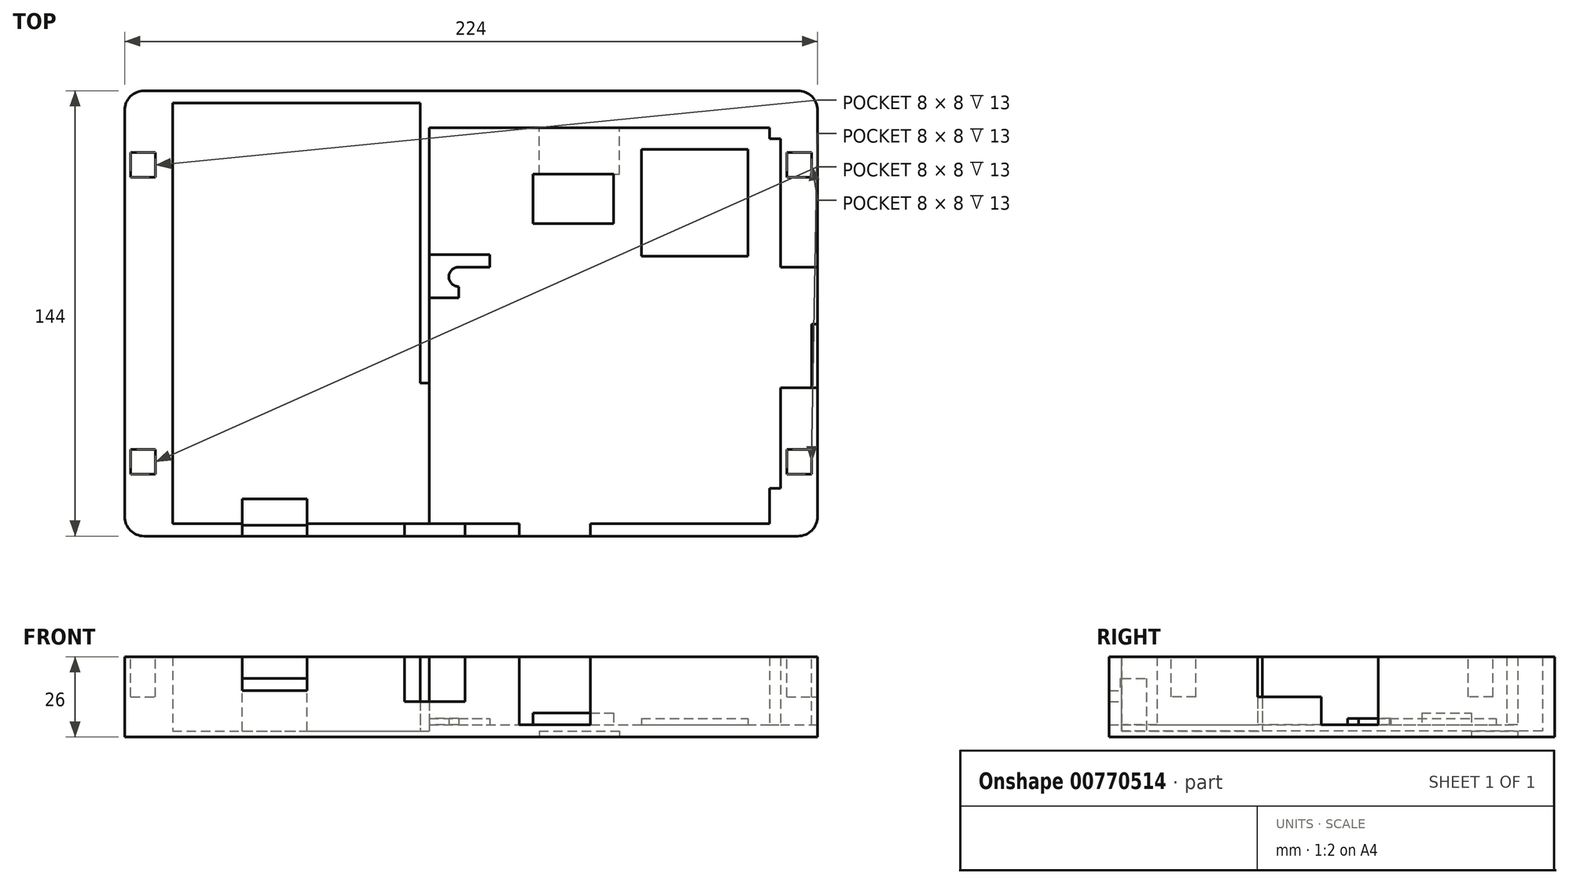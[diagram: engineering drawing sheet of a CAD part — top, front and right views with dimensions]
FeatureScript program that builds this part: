
annotation { "Feature Type Name" : "Feature", "Feature Type Description" : "" }
export const myFeature = defineFeature(function(context is Context, id is Id, definition is map)
    precondition{}
    {
        {
            var Q0;
            Q0=qCreatedBy(makeId("Top.planeOp"),FACE);
            var sketch = newSketch(context, id + "F0", { "sketchPlane" : qUnion([Q0])});
            skLineSegment(sketch, "E0.bottom", {"start": v(-224, 0) * mm, "end": v(0, 0) * mm});
            skLineSegment(sketch, "E0.top", {"start": v(-224, 144) * mm, "end": v(0, 144) * mm});
            skLineSegment(sketch, "E0.left", {"start": v(-224, 0) * mm, "end": v(-224, 144) * mm});
            skLineSegment(sketch, "E0.right", {"start": v(0, 0) * mm, "end": v(0, 144) * mm});
            skLineSegment(sketch, "E1.bottom", {"start": v(-208.5, 140) * mm, "end": v(-128.5, 140) * mm});
            skLineSegment(sketch, "E1.top", {"start": v(-208.5, 4) * mm, "end": v(-186, 4) * mm});
            skLineSegment(sketch, "E1.left", {"start": v(-208.5, 140) * mm, "end": v(-208.5, 4) * mm});
            skLineSegment(sketch, "E1.right", {"start": v(-12, 128.5) * mm, "end": v(-12, 15.5) * mm});
            skLineSegment(sketch, "E2", {"start": v(-128.5, 140) * mm, "end": v(-128.5, 49.5) * mm});
            skLineSegment(sketch, "E3", {"start": v(-128.5, 49.5) * mm, "end": v(-125.5, 49.5) * mm});
            skLineSegment(sketch, "E4", {"start": v(-125.5, 49.5) * mm, "end": v(-125.5, 132) * mm});
            skLineSegment(sketch, "E5.bottom", {"start": v(-222, 124) * mm, "end": v(-214, 124) * mm});
            skLineSegment(sketch, "E5.top", {"start": v(-222, 116) * mm, "end": v(-214, 116) * mm});
            skLineSegment(sketch, "E5.left", {"start": v(-222, 124) * mm, "end": v(-222, 116) * mm});
            skLineSegment(sketch, "E5.right", {"start": v(-214, 124) * mm, "end": v(-214, 116) * mm});
            skLineSegment(sketch, "E6.bottom", {"start": v(-222, 28) * mm, "end": v(-214, 28) * mm});
            skLineSegment(sketch, "E6.top", {"start": v(-222, 20) * mm, "end": v(-214, 20) * mm});
            skLineSegment(sketch, "E6.left", {"start": v(-222, 28) * mm, "end": v(-222, 20) * mm});
            skLineSegment(sketch, "E6.right", {"start": v(-214, 28) * mm, "end": v(-214, 20) * mm});
            skLineSegment(sketch, "E7", {"start": v(-165, 0) * mm, "end": v(-165, 12) * mm});
            skLineSegment(sketch, "E8.trimOffspring", {"start": v(-165, 4) * mm, "end": v(-15.5, 4) * mm});
            skLineSegment(sketch, "E9", {"start": v(-186, 0) * mm, "end": v(-186, 12) * mm});
            skLineSegment(sketch, "E10", {"start": v(-175.5, 30.08) * mm, "end": v(-175.5, -46.23) * mm, "construction": true});
            skLineSegment(sketch, "E11", {"start": v(-186, 12) * mm, "end": v(-165, 12) * mm});
            skLineSegment(sketch, "E12", {"start": v(-133.5, 4) * mm, "end": v(-133.5, 0) * mm});
            skLineSegment(sketch, "E13", {"start": v(-114, 4) * mm, "end": v(-114, 0) * mm});
            skLineSegment(sketch, "E14", {"start": v(-73.4, 4) * mm, "end": v(-73.4, 0) * mm});
            skLineSegment(sketch, "E15", {"start": v(-96.4, 4) * mm, "end": v(-96.4, 0) * mm});
            skLineSegment(sketch, "E16.bottom", {"start": v(-10, 28) * mm, "end": v(-2, 28) * mm});
            skLineSegment(sketch, "E16.top", {"start": v(-10, 20) * mm, "end": v(-2, 20) * mm});
            skLineSegment(sketch, "E16.left", {"start": v(-10, 28) * mm, "end": v(-10, 20) * mm});
            skLineSegment(sketch, "E16.right", {"start": v(-2, 28) * mm, "end": v(-2, 20) * mm});
            skLineSegment(sketch, "E17.bottom", {"start": v(-10, 124) * mm, "end": v(-2, 124) * mm});
            skLineSegment(sketch, "E17.top", {"start": v(-10, 116) * mm, "end": v(-2, 116) * mm});
            skLineSegment(sketch, "E17.left", {"start": v(-10, 124) * mm, "end": v(-10, 116) * mm});
            skLineSegment(sketch, "E17.right", {"start": v(-2, 124) * mm, "end": v(-2, 116) * mm});
            skLineSegment(sketch, "E18", {"start": v(-15.5, 132) * mm, "end": v(-15.5, 128.5) * mm});
            skLineSegment(sketch, "E19", {"start": v(-15.5, 128.5) * mm, "end": v(-12, 128.5) * mm});
            skLineSegment(sketch, "E20", {"start": v(-12, 15.5) * mm, "end": v(-15.5, 15.5) * mm});
            skLineSegment(sketch, "E21", {"start": v(-15.5, 15.5) * mm, "end": v(-15.5, 4) * mm});
            skLineSegment(sketch, "E22", {"start": v(-15.5, 132) * mm, "end": v(-125.5, 132) * mm});
            skLineSegment(sketch, "E23.bottom", {"start": v(-57, 125) * mm, "end": v(-22, 125) * mm});
            skLineSegment(sketch, "E23.top", {"start": v(-57, 90.5) * mm, "end": v(-22, 90.5) * mm});
            skLineSegment(sketch, "E23.left", {"start": v(-57, 125) * mm, "end": v(-57, 90.5) * mm});
            skLineSegment(sketch, "E24.bottom", {"start": v(-60, 89) * mm, "end": v(-17.5, 89) * mm, "construction": true});
            skLineSegment(sketch, "E24.top", {"start": v(-60, 132) * mm, "end": v(-17.5, 132) * mm, "construction": true});
            skLineSegment(sketch, "E24.left", {"start": v(-60, 89) * mm, "end": v(-60, 132) * mm, "construction": true});
            skLineSegment(sketch, "E24.right", {"start": v(-17.5, 89) * mm, "end": v(-17.5, 132) * mm, "construction": true});
            skLineSegment(sketch, "E25.bottom", {"start": v(-90, 96) * mm, "end": v(-64, 96) * mm});
            skLineSegment(sketch, "E25.top", {"start": v(-90, 132) * mm, "end": v(-64, 132) * mm});
            skLineSegment(sketch, "E25.left", {"start": v(-90, 96) * mm, "end": v(-90, 132) * mm});
            skLineSegment(sketch, "E25.right", {"start": v(-64, 96) * mm, "end": v(-64, 132) * mm});
            skLineSegment(sketch, "E26", {"start": v(-125.5, 49.5) * mm, "end": v(-116, 49.5) * mm});
            skLineSegment(sketch, "E27", {"start": v(-116, 87) * mm, "end": v(-116, 49.5) * mm});
            skLineSegment(sketch, "E28", {"start": v(-116, 87) * mm, "end": v(-125.5, 87) * mm});
            skLineSegment(sketch, "E29", {"start": v(-116, 87) * mm, "end": v(0, 87) * mm});
            skLineSegment(sketch, "E30", {"start": v(-12, 50) * mm, "end": v(0, 50) * mm});
            skLineSegment(sketch, "E31", {"start": v(-128.5, 49.5) * mm, "end": v(-128.5, 4) * mm});
            skPoint(sketch, "E32.startSnap0", {"position": v(-112, 144) * mm});
            skLineSegment(sketch, "E33.bottom", {"start": v(-90, 101) * mm, "end": v(-64, 101) * mm});
            skLineSegment(sketch, "E33.top", {"start": v(-90, 117) * mm, "end": v(-64, 117) * mm});
            skLineSegment(sketch, "E33.left", {"start": v(-90, 101) * mm, "end": v(-90, 117) * mm});
            skLineSegment(sketch, "E33.right", {"start": v(-64, 101) * mm, "end": v(-64, 117) * mm});
            skLineSegment(sketch, "E34", {"start": v(-22, 125) * mm, "end": v(-22, 90.5) * mm});
            skLineSegment(sketch, "E35", {"start": v(-196, 0) * mm, "end": v(-196, 4) * mm, "construction": true});
            skSolve(sketch);
        }
        {
            var Q0;
            {var subQ14=sQuery(id+"F0.wireOp",EDGE,"E0.top");Q0=makeQuery(id+"F0.imprint","IMPRINT",FACE,{"disambiguationData":[TD([[makeQuery(id+"F0.imprint","IMPRINT",EDGE,{"derivedFrom":subQ14}),-1.0]])]});}
            var Q1;
            Q1=makeQuery(id+"F0.imprint","IMPRINT",FACE,{"disambiguationData":[TD([[makeQuery(id+"F0.imprint","IMPRINT",EDGE,{"derivedFrom":sQuery(id+"F0.wireOp",EDGE,"E1.bottom")}),-1.0]])]});
            var Q2;
            {var subQ5=sQuery(id+"F0.wireOp",EDGE,"E1.top");Q2=makeQuery(id+"F0.imprint","IMPRINT",FACE,{"disambiguationData":[TD([[makeQuery(id+"F0.imprint","IMPRINT",EDGE,{"derivedFrom":subQ5}),-1.0]])]});}
            var Q3;
            {var subQ0=sQuery(id+"F0.wireOp",EDGE,"E12");Q3=makeQuery(id+"F0.imprint","IMPRINT",FACE,{"disambiguationData":[TD([[makeQuery(id+"F0.imprint","IMPRINT",EDGE,{"derivedFrom":subQ0}),1.0]])]});}
            var Q4;
            {var subQ0=sQuery(id+"F0.wireOp",EDGE,"E15");Q4=makeQuery(id+"F0.imprint","IMPRINT",FACE,{"disambiguationData":[TD([[makeQuery(id+"F0.imprint","IMPRINT",EDGE,{"derivedFrom":subQ0}),-1.0]])]});}
            var Q5;
            {var subQ3=sQuery(id+"F0.wireOp",EDGE,"E12");Q5=makeQuery(id+"F0.imprint","IMPRINT",FACE,{"disambiguationData":[TD([[makeQuery(id+"F0.imprint","IMPRINT",EDGE,{"derivedFrom":subQ3}),-1.0]])]});}
            var Q6;
            {var subQ7=sQuery(id+"F0.wireOp",EDGE,"E11");Q6=makeQuery(id+"F0.imprint","IMPRINT",FACE,{"disambiguationData":[TD([[makeQuery(id+"F0.imprint","IMPRINT",EDGE,{"derivedFrom":subQ7}),-1.0]])]});}
            var Q7;
            {var subQ0=sQuery(id+"F0.wireOp",EDGE,"E26");Q7=makeQuery(id+"F0.imprint","IMPRINT",FACE,{"disambiguationData":[TD([[makeQuery(id+"F0.imprint","IMPRINT",EDGE,{"derivedFrom":subQ0}),1.0]])]});}
            var Q8;
            {var subQ11=sQuery(id+"F0.wireOp",EDGE,"E18");Q8=makeQuery(id+"F0.imprint","IMPRINT",FACE,{"disambiguationData":[TD([[makeQuery(id+"F0.imprint","IMPRINT",EDGE,{"derivedFrom":subQ11}),-1.0]])]});}
            var Q9;
            {var subQ0=sQuery(id+"F0.wireOp",EDGE,"E25.top");Q9=makeQuery(id+"F0.imprint","IMPRINT",FACE,{"disambiguationData":[TD([[makeQuery(id+"F0.imprint","IMPRINT",EDGE,{"derivedFrom":subQ0}),-1.0]])]});}
            var Q10;
            Q10=makeQuery(id+"F0.imprint","IMPRINT",FACE,{"disambiguationData":[TD([[makeQuery(id+"F0.imprint","IMPRINT",EDGE,{"derivedFrom":sQuery(id+"F0.wireOp",EDGE,"E33.bottom")}),1.0]])]});
            var Q11;
            {var subQ0=sQuery(id+"F0.wireOp",EDGE,"E25.bottom");Q11=makeQuery(id+"F0.imprint","IMPRINT",FACE,{"disambiguationData":[TD([[makeQuery(id+"F0.imprint","IMPRINT",EDGE,{"derivedFrom":subQ0}),1.0]])]});}
            var Q12;
            Q12=makeQuery(id+"F0.imprint","IMPRINT",FACE,{"disambiguationData":[TD([[makeQuery(id+"F0.imprint","IMPRINT",EDGE,{"derivedFrom":sQuery(id+"F0.wireOp",EDGE,"E23.bottom")}),-1.0]])]});
            var Q13;
            Q13=makeQuery(id+"F0.imprint","IMPRINT",FACE,{"disambiguationData":[TD([[makeQuery(id+"F0.imprint","IMPRINT",EDGE,{"derivedFrom":sQuery(id+"F0.wireOp",EDGE,"E17.bottom")}),-1.0]])]});
            var Q14;
            Q14=makeQuery(id+"F0.imprint","IMPRINT",FACE,{"disambiguationData":[TD([[makeQuery(id+"F0.imprint","IMPRINT",EDGE,{"derivedFrom":sQuery(id+"F0.wireOp",EDGE,"E5.bottom")}),-1.0]])]});
            var Q15;
            Q15=makeQuery(id+"F0.imprint","IMPRINT",FACE,{"disambiguationData":[TD([[makeQuery(id+"F0.imprint","IMPRINT",EDGE,{"derivedFrom":sQuery(id+"F0.wireOp",EDGE,"E6.bottom")}),-1.0]])]});
            var Q16;
            {var subQ0=sQuery(id+"F0.wireOp",EDGE,"E30");var subQ1=sQuery(id+"F0.wireOp",EDGE,"E0.right");var subQ2=makeQuery(id+"F0.imprint","INTERSECT",VERTEX,{"derivedFrom":[subQ1,subQ0]});Q16=makeQuery(id+"F0.imprint","IMPRINT",FACE,{"disambiguationData":[TD([[makeQuery(id+"F0.imprint","IMPRINT",EDGE,{"disambiguationData":[TD([[subQ2,-1.0]])],"derivedFrom":subQ1}),1.0]])]});}
            var Q17;
            Q17=makeQuery(id+"F0.imprint","IMPRINT",FACE,{"disambiguationData":[TD([[makeQuery(id+"F0.imprint","IMPRINT",EDGE,{"derivedFrom":sQuery(id+"F0.wireOp",EDGE,"E3")}),-1.0]])]});
            var Q18;
            {var subQ6=sQuery(id+"F0.wireOp",EDGE,"E14");Q18=makeQuery(id+"F0.imprint","IMPRINT",FACE,{"disambiguationData":[TD([[makeQuery(id+"F0.imprint","IMPRINT",EDGE,{"derivedFrom":subQ6}),1.0]])]});}
            var Q19;
            Q19=makeQuery(id+"F0.imprint","IMPRINT",FACE,{"disambiguationData":[TD([[makeQuery(id+"F0.imprint","IMPRINT",EDGE,{"derivedFrom":sQuery(id+"F0.wireOp",EDGE,"E16.bottom")}),-1.0]])]});
            var Q20;
            {var subQ0=sQuery(id+"F0.wireOp",EDGE,"E14");Q20=makeQuery(id+"F0.imprint","IMPRINT",FACE,{"disambiguationData":[TD([[makeQuery(id+"F0.imprint","IMPRINT",EDGE,{"derivedFrom":subQ0}),-1.0]])]});}
            extrude(context, id + "F1", {"entities" : qUnion([Q0, Q1, Q2, Q3, Q4, Q5, Q6, Q7, Q8, Q9, Q10, Q11, Q12, Q13, Q14, Q15, Q16, Q17, Q18, Q19, Q20]), "depth" : 2 * mm, "offsetDistance" : 25 * mm});
        }
        {
            var Q0;
            Q0=makeQuery(id+"F1.opExtrude","CAP_FACE",FACE,{"disambiguationData":[OSD([sQuery(id+"F0.wireOp",EDGE,"E0.bottom"),sQuery(id+"F0.wireOp",EDGE,"E0.top"),sQuery(id+"F0.wireOp",EDGE,"E0.left"),sQuery(id+"F0.wireOp",EDGE,"E0.right")])],"isStart":false});
            var sketch = newSketch(context, id + "F2", { "sketchPlane" : qUnion([Q0])});
            skLineSegment(sketch, "E36.bottom", {"start": v(-224, 0) * mm, "end": v(0, 0) * mm});
            skLineSegment(sketch, "E36.top", {"start": v(-224, 144) * mm, "end": v(0, 144) * mm});
            skLineSegment(sketch, "E36.left", {"start": v(-224, 0) * mm, "end": v(-224, 144) * mm});
            skLineSegment(sketch, "E36.right", {"start": v(0, 0) * mm, "end": v(0, 144) * mm});
            skLineSegment(sketch, "E37", {"start": v(-208.5, 140) * mm, "end": v(-208.5, 4) * mm});
            skLineSegment(sketch, "E38", {"start": v(-208.5, 4) * mm, "end": v(-15.5, 4) * mm});
            skLineSegment(sketch, "E39", {"start": v(-208.5, 140) * mm, "end": v(-128.5, 140) * mm});
            skLineSegment(sketch, "E40", {"start": v(-128.5, 140) * mm, "end": v(-128.5, 49.5) * mm});
            skLineSegment(sketch, "E41", {"start": v(-128.5, 49.5) * mm, "end": v(-125.5, 49.5) * mm});
            skLineSegment(sketch, "E42", {"start": v(-125.5, 49.5) * mm, "end": v(-125.5, 132) * mm});
            skLineSegment(sketch, "E43", {"start": v(-125.5, 132) * mm, "end": v(-15.5, 132) * mm});
            skLineSegment(sketch, "E44", {"start": v(-15.5, 132) * mm, "end": v(-15.5, 128.5) * mm});
            skLineSegment(sketch, "E45", {"start": v(-15.5, 128.5) * mm, "end": v(-12, 128.5) * mm});
            skLineSegment(sketch, "E46", {"start": v(-12, 128.5) * mm, "end": v(-12, 87) * mm});
            skLineSegment(sketch, "E47", {"start": v(-12, 87) * mm, "end": v(-2, 87) * mm});
            skLineSegment(sketch, "E48", {"start": v(-2, 87) * mm, "end": v(-2, 50) * mm});
            skLineSegment(sketch, "E49", {"start": v(-2, 50) * mm, "end": v(-12, 50) * mm, "construction": true});
            skLineSegment(sketch, "E50", {"start": v(-12, 48) * mm, "end": v(-12, 15.5) * mm});
            skLineSegment(sketch, "E51", {"start": v(-12, 15.5) * mm, "end": v(-15.5, 15.5) * mm});
            skLineSegment(sketch, "E52", {"start": v(-15.5, 15.5) * mm, "end": v(-15.5, 4) * mm});
            skLineSegment(sketch, "E53", {"start": v(-12, 48) * mm, "end": v(-2, 48) * mm});
            skLineSegment(sketch, "E54", {"start": v(-2, 48) * mm, "end": v(-2, 50) * mm});
            skSolve(sketch);
        }
        {
            var Q0;
            Q0=qSketchRegion(id+"F2",true);
            extrude(context, id + "F3", {"entities" : qUnion([Q0]), "operationType" : NewBodyOperationType.ADD, "depth" : 24 * mm, "offsetDistance" : 25 * mm});
        }
        {
            var Q0;
            Q0=makeQuery(id+"F3.opExtrude","CAP_FACE",FACE,{"disambiguationData":[OSD([sQuery(id+"F2.wireOp",EDGE,"E36.bottom"),sQuery(id+"F2.wireOp",EDGE,"E36.top"),sQuery(id+"F2.wireOp",EDGE,"E36.left"),sQuery(id+"F2.wireOp",EDGE,"E36.right"),sQuery(id+"F2.wireOp",EDGE,"E37"),sQuery(id+"F2.wireOp",EDGE,"E38"),sQuery(id+"F2.wireOp",EDGE,"E39"),sQuery(id+"F2.wireOp",EDGE,"E40"),sQuery(id+"F2.wireOp",EDGE,"E41"),sQuery(id+"F2.wireOp",EDGE,"E42"),sQuery(id+"F2.wireOp",EDGE,"E43"),sQuery(id+"F2.wireOp",EDGE,"E44"),sQuery(id+"F2.wireOp",EDGE,"E45"),sQuery(id+"F2.wireOp",EDGE,"E46"),sQuery(id+"F2.wireOp",EDGE,"E47"),sQuery(id+"F2.wireOp",EDGE,"E48"),sQuery(id+"F2.wireOp",EDGE,"E49"),sQuery(id+"F2.wireOp",EDGE,"E50"),sQuery(id+"F2.wireOp",EDGE,"E51"),sQuery(id+"F2.wireOp",EDGE,"E52")])],"isStart":false});
            var sketch = newSketch(context, id + "F4", { "sketchPlane" : qUnion([Q0])});
            skLineSegment(sketch, "E55.bottom", {"start": v(-186, 0) * mm, "end": v(-165, 0) * mm});
            skLineSegment(sketch, "E55.top", {"start": v(-186, 4) * mm, "end": v(-165, 4) * mm});
            skLineSegment(sketch, "E55.left", {"start": v(-186, 0) * mm, "end": v(-186, 4) * mm});
            skLineSegment(sketch, "E55.right", {"start": v(-165, 0) * mm, "end": v(-165, 4) * mm});
            skSolve(sketch);
        }
        {
            var Q0;
            Q0=qSketchRegion(id+"F4",true);
            extrude(context, id + "F5", {"entities" : qUnion([Q0]), "operationType" : NewBodyOperationType.REMOVE, "oppositeDirection" : true, "depth" : 11 * mm, "offsetDistance" : 25 * mm});
        }
        {
            var Q0;
            Q0=makeQuery(id+"F1.opExtrude","CAP_FACE",FACE,{"disambiguationData":[OSD([sQuery(id+"F0.wireOp",EDGE,"E0.bottom"),sQuery(id+"F0.wireOp",EDGE,"E0.top"),sQuery(id+"F0.wireOp",EDGE,"E0.left"),sQuery(id+"F0.wireOp",EDGE,"E0.right")])],"isStart":false});
            var sketch = newSketch(context, id + "F6", { "sketchPlane" : qUnion([Q0])});
            skLineSegment(sketch, "E56.bottom", {"start": v(-186, 3.5) * mm, "end": v(-165, 3.5) * mm});
            skLineSegment(sketch, "E56.top", {"start": v(-186, 12) * mm, "end": v(-165, 12) * mm});
            skLineSegment(sketch, "E56.left", {"start": v(-186, 3.5) * mm, "end": v(-186, 12) * mm});
            skLineSegment(sketch, "E56.right", {"start": v(-165, 3.5) * mm, "end": v(-165, 12) * mm});
            skSolve(sketch);
        }
        {
            var Q0;
            Q0=qSketchRegion(id+"F6",true);
            extrude(context, id + "F7", {"entities" : qUnion([Q0]), "operationType" : NewBodyOperationType.ADD, "depth" : 17 * mm, "offsetDistance" : 25 * mm});
        }
        {
            var Q0;
            Q0=makeQuery(id+"F3.boolean.opBoolean","MERGE",EDGE,{"derivedFrom":[makeQuery(id+"F1.opExtrude","SWEPT_EDGE",EDGE,{"disambiguationData":[OSD([sQuery(id+"F0.wireOp",EDGE,"E0.bottom"),sQuery(id+"F0.wireOp",EDGE,"E0.left")])]}),makeQuery(id+"F3.opExtrude","SWEPT_EDGE",EDGE,{"disambiguationData":[OSD([sQuery(id+"F2.wireOp",EDGE,"E36.bottom"),sQuery(id+"F2.wireOp",EDGE,"E36.left")])]})]});
            var Q1;
            Q1=makeQuery(id+"F3.boolean.opBoolean","MERGE",EDGE,{"derivedFrom":[makeQuery(id+"F1.opExtrude","SWEPT_EDGE",EDGE,{"disambiguationData":[OSD([sQuery(id+"F0.wireOp",EDGE,"E0.bottom"),sQuery(id+"F0.wireOp",EDGE,"E0.right")])]}),makeQuery(id+"F3.opExtrude","SWEPT_EDGE",EDGE,{"disambiguationData":[OSD([sQuery(id+"F2.wireOp",EDGE,"E36.bottom"),sQuery(id+"F2.wireOp",EDGE,"E36.right")])]})]});
            var Q2;
            Q2=makeQuery(id+"F3.boolean.opBoolean","MERGE",EDGE,{"derivedFrom":[makeQuery(id+"F1.opExtrude","SWEPT_EDGE",EDGE,{"disambiguationData":[OSD([sQuery(id+"F0.wireOp",EDGE,"E0.top"),sQuery(id+"F0.wireOp",EDGE,"E0.right")])]}),makeQuery(id+"F3.opExtrude","SWEPT_EDGE",EDGE,{"disambiguationData":[OSD([sQuery(id+"F2.wireOp",EDGE,"E36.top"),sQuery(id+"F2.wireOp",EDGE,"E36.right")])]})]});
            var Q3;
            Q3=makeQuery(id+"F3.boolean.opBoolean","MERGE",EDGE,{"derivedFrom":[makeQuery(id+"F1.opExtrude","SWEPT_EDGE",EDGE,{"disambiguationData":[OSD([sQuery(id+"F0.wireOp",EDGE,"E0.top"),sQuery(id+"F0.wireOp",EDGE,"E0.left")])]}),makeQuery(id+"F3.opExtrude","SWEPT_EDGE",EDGE,{"disambiguationData":[OSD([sQuery(id+"F2.wireOp",EDGE,"E36.top"),sQuery(id+"F2.wireOp",EDGE,"E36.left")])]})]});
            fillet(context, id + "F8", {"entities" : qUnion([Q0, Q1, Q2, Q3]), "radius" : 6.35 * mm, "tangentPropagation" : true, "allowEdgeOverflow" : false});
        }
        {
            var Q0;
            Q0=makeQuery(id+"F1.opExtrude","CAP_FACE",FACE,{"disambiguationData":[OSD([sQuery(id+"F0.wireOp",EDGE,"E0.bottom"),sQuery(id+"F0.wireOp",EDGE,"E0.top"),sQuery(id+"F0.wireOp",EDGE,"E0.left"),sQuery(id+"F0.wireOp",EDGE,"E0.right")])],"isStart":false});
            var sketch = newSketch(context, id + "F9", { "sketchPlane" : qUnion([Q0])});
            skLineSegment(sketch, "E57.bottom", {"start": v(-57, 90.5) * mm, "end": v(-22.5, 90.5) * mm});
            skLineSegment(sketch, "E57.top", {"start": v(-57, 125) * mm, "end": v(-22.5, 125) * mm});
            skLineSegment(sketch, "E57.left", {"start": v(-57, 90.5) * mm, "end": v(-57, 125) * mm});
            skLineSegment(sketch, "E57.right", {"start": v(-22.5, 90.5) * mm, "end": v(-22.5, 125) * mm});
            skLineSegment(sketch, "E58.bottom", {"start": v(-60, 87) * mm, "end": v(-15, 87) * mm, "construction": true});
            skLineSegment(sketch, "E58.top", {"start": v(-60, 132) * mm, "end": v(-15, 132) * mm, "construction": true});
            skLineSegment(sketch, "E58.left", {"start": v(-60, 87) * mm, "end": v(-60, 132) * mm, "construction": true});
            skLineSegment(sketch, "E58.right", {"start": v(-15, 87) * mm, "end": v(-15, 132) * mm, "construction": true});
            skSolve(sketch);
        }
        {
            var Q0;
            Q0=qSketchRegion(id+"F9",true);
            extrude(context, id + "F10", {"entities" : qUnion([Q0]), "operationType" : NewBodyOperationType.ADD, "depth" : 4 * mm, "offsetDistance" : 25 * mm});
        }
        {
            var Q0;
            Q0=makeQuery(id+"F1.opExtrude","CAP_FACE",FACE,{"disambiguationData":[OSD([sQuery(id+"F0.wireOp",EDGE,"E0.bottom"),sQuery(id+"F0.wireOp",EDGE,"E0.top"),sQuery(id+"F0.wireOp",EDGE,"E0.left"),sQuery(id+"F0.wireOp",EDGE,"E0.right")])],"isStart":false});
            var sketch = newSketch(context, id + "F11", { "sketchPlane" : qUnion([Q0])});
            skLineSegment(sketch, "E59.bottom", {"start": v(-92, 101) * mm, "end": v(-66, 101) * mm});
            skLineSegment(sketch, "E59.top", {"start": v(-92, 117) * mm, "end": v(-66, 117) * mm});
            skLineSegment(sketch, "E59.left", {"start": v(-92, 101) * mm, "end": v(-92, 117) * mm});
            skLineSegment(sketch, "E59.right", {"start": v(-66, 101) * mm, "end": v(-66, 117) * mm});
            skSolve(sketch);
        }
        {
            var Q0;
            Q0=qSketchRegion(id+"F11",true);
            extrude(context, id + "F12", {"entities" : qUnion([Q0]), "operationType" : NewBodyOperationType.ADD, "depth" : 5.8 * mm, "offsetDistance" : 25 * mm});
        }
        {
            var Q0;
            Q0=makeQuery(id+"F1.opExtrude","CAP_FACE",FACE,{"disambiguationData":[OSD([sQuery(id+"F0.wireOp",EDGE,"E0.bottom"),sQuery(id+"F0.wireOp",EDGE,"E0.top"),sQuery(id+"F0.wireOp",EDGE,"E0.left"),sQuery(id+"F0.wireOp",EDGE,"E0.right")])],"isStart":false});
            var sketch = newSketch(context, id + "F13", { "sketchPlane" : qUnion([Q0])});
            skLineSegment(sketch, "E60", {"start": v(-116, 87) * mm, "end": v(-106, 87) * mm});
            skLineSegment(sketch, "E61", {"start": v(-116, 77) * mm, "end": v(-125.5, 77) * mm});
            skLineSegment(sketch, "E62", {"start": v(-125.5, 77) * mm, "end": v(-125.5, 91) * mm});
            skLineSegment(sketch, "E63", {"start": v(-125.5, 91) * mm, "end": v(-106, 91) * mm});
            skLineSegment(sketch, "E64", {"start": v(-106, 91) * mm, "end": v(-106, 87) * mm});
            skArc(sketch, "E65", {"start": v(-116, 87) * mm, "mid": v(-119.18, 83.83) * mm, "end": v(-116, 80.65) * mm});
            skLineSegment(sketch, "E66", {"start": v(-116, 77) * mm, "end": v(-116, 80.65) * mm});
            skSolve(sketch);
        }
        {
            var Q0;
            Q0=qSketchRegion(id+"F13",true);
            extrude(context, id + "F14", {"entities" : qUnion([Q0]), "operationType" : NewBodyOperationType.ADD, "depth" : 4 * mm, "offsetDistance" : 25 * mm});
        }
        {
            var Q0;
            Q0=makeQuery(id+"F3.opExtrude","CAP_FACE",FACE,{"disambiguationData":[OSD([sQuery(id+"F2.wireOp",EDGE,"E36.bottom"),sQuery(id+"F2.wireOp",EDGE,"E36.top"),sQuery(id+"F2.wireOp",EDGE,"E36.left"),sQuery(id+"F2.wireOp",EDGE,"E36.right"),sQuery(id+"F2.wireOp",EDGE,"E37"),sQuery(id+"F2.wireOp",EDGE,"E38"),sQuery(id+"F2.wireOp",EDGE,"E39"),sQuery(id+"F2.wireOp",EDGE,"E40"),sQuery(id+"F2.wireOp",EDGE,"E41"),sQuery(id+"F2.wireOp",EDGE,"E42"),sQuery(id+"F2.wireOp",EDGE,"E43"),sQuery(id+"F2.wireOp",EDGE,"E44"),sQuery(id+"F2.wireOp",EDGE,"E45"),sQuery(id+"F2.wireOp",EDGE,"E46"),sQuery(id+"F2.wireOp",EDGE,"E47"),sQuery(id+"F2.wireOp",EDGE,"E48"),sQuery(id+"F2.wireOp",EDGE,"E50"),sQuery(id+"F2.wireOp",EDGE,"E51"),sQuery(id+"F2.wireOp",EDGE,"E52"),sQuery(id+"F2.wireOp",EDGE,"E53"),sQuery(id+"F2.wireOp",EDGE,"E54")])],"isStart":false});
            var sketch = newSketch(context, id + "F15", { "sketchPlane" : qUnion([Q0])});
            skLineSegment(sketch, "E67.bottom", {"start": v(-133.5, 0) * mm, "end": v(-114, 0) * mm});
            skLineSegment(sketch, "E67.top", {"start": v(-133.5, 4) * mm, "end": v(-114, 4) * mm});
            skLineSegment(sketch, "E67.left", {"start": v(-133.5, 0) * mm, "end": v(-133.5, 4) * mm});
            skLineSegment(sketch, "E67.right", {"start": v(-114, 0) * mm, "end": v(-114, 4) * mm});
            skSolve(sketch);
        }
        {
            var Q0;
            Q0=qSketchRegion(id+"F15",true);
            extrude(context, id + "F16", {"entities" : qUnion([Q0]), "operationType" : NewBodyOperationType.REMOVE, "oppositeDirection" : true, "depth" : 14.5 * mm, "offsetDistance" : 25 * mm});
        }
        {
            var Q0;
            {var subQ0=sQuery(id+"F2.wireOp",EDGE,"E50");var subQ1=sQuery(id+"F2.wireOp",EDGE,"E36.right");var subQ2=sQuery(id+"F2.wireOp",EDGE,"E36.top");var subQ4=sQuery(id+"F0.wireOp",EDGE,"E0.top");var subQ5=sQuery(id+"F2.wireOp",EDGE,"E54");var subQ6=sQuery(id+"F2.wireOp",EDGE,"E48");var subQ7=sQuery(id+"F2.wireOp",EDGE,"E36.left");var subQ9=sQuery(id+"F2.wireOp",EDGE,"E47");var subQ10=sQuery(id+"F2.wireOp",EDGE,"E36.bottom");var subQ12=sQuery(id+"F2.wireOp",EDGE,"E46");var subQ13=sQuery(id+"F2.wireOp",EDGE,"E45");var subQ14=sQuery(id+"F2.wireOp",EDGE,"E44");var subQ15=sQuery(id+"F2.wireOp",EDGE,"E43");var subQ16=sQuery(id+"F2.wireOp",EDGE,"E42");var subQ17=sQuery(id+"F2.wireOp",EDGE,"E41");var subQ18=sQuery(id+"F2.wireOp",EDGE,"E40");var subQ19=sQuery(id+"F2.wireOp",EDGE,"E39");var subQ20=sQuery(id+"F2.wireOp",EDGE,"E51");var subQ21=sQuery(id+"F2.wireOp",EDGE,"E37");var subQ22=sQuery(id+"F2.wireOp",EDGE,"E38");var subQ23=sQuery(id+"F2.wireOp",EDGE,"E52");var subQ24=sQuery(id+"F2.wireOp",EDGE,"E53");Q0=makeQuery(id+"F16.boolean.opBoolean","SPLIT",FACE,{"disambiguationData":[TD([makeQuery(id+"F1.opExtrude","SWEPT_FACE",FACE,{"disambiguationData":[OSD([subQ4])]})])],"derivedFrom":makeQuery(id+"F3.opExtrude","CAP_FACE",FACE,{"disambiguationData":[OSD([subQ10,subQ2,subQ7,subQ1,subQ21,subQ22,subQ19,subQ18,subQ17,subQ16,subQ15,subQ14,subQ13,subQ12,subQ9,subQ6,subQ0,subQ20,subQ23,subQ24,subQ5])],"isStart":false})});}
            var sketch = newSketch(context, id + "F17", { "sketchPlane" : qUnion([Q0])});
            skLineSegment(sketch, "E68.bottom", {"start": v(-222, 124) * mm, "end": v(-214, 124) * mm});
            skLineSegment(sketch, "E68.top", {"start": v(-222, 116) * mm, "end": v(-214, 116) * mm});
            skLineSegment(sketch, "E68.left", {"start": v(-222, 124) * mm, "end": v(-222, 116) * mm});
            skLineSegment(sketch, "E68.right", {"start": v(-214, 124) * mm, "end": v(-214, 116) * mm});
            skLineSegment(sketch, "E69.bottom", {"start": v(-10, 124) * mm, "end": v(-2, 124) * mm});
            skLineSegment(sketch, "E69.top", {"start": v(-10, 116) * mm, "end": v(-2, 116) * mm});
            skLineSegment(sketch, "E69.left", {"start": v(-10, 124) * mm, "end": v(-10, 116) * mm});
            skLineSegment(sketch, "E69.right", {"start": v(-2, 124) * mm, "end": v(-2, 116) * mm});
            skLineSegment(sketch, "E70.bottom", {"start": v(-222, 28) * mm, "end": v(-214, 28) * mm});
            skLineSegment(sketch, "E70.top", {"start": v(-222, 20) * mm, "end": v(-214, 20) * mm});
            skLineSegment(sketch, "E70.left", {"start": v(-222, 28) * mm, "end": v(-222, 20) * mm});
            skLineSegment(sketch, "E70.right", {"start": v(-214, 28) * mm, "end": v(-214, 20) * mm});
            skLineSegment(sketch, "E71.bottom", {"start": v(-10, 28) * mm, "end": v(-2, 28) * mm});
            skLineSegment(sketch, "E71.top", {"start": v(-10, 20) * mm, "end": v(-2, 20) * mm});
            skLineSegment(sketch, "E71.left", {"start": v(-10, 28) * mm, "end": v(-10, 20) * mm});
            skLineSegment(sketch, "E71.right", {"start": v(-2, 28) * mm, "end": v(-2, 20) * mm});
            skSolve(sketch);
        }
        {
            var Q0;
            Q0=qSketchRegion(id+"F17",true);
            extrude(context, id + "F18", {"entities" : qUnion([Q0]), "operationType" : NewBodyOperationType.REMOVE, "oppositeDirection" : true, "depth" : 13 * mm, "offsetDistance" : 25 * mm});
        }
        {
            var Q0;
            {var subQ0=sQuery(id+"F2.wireOp",EDGE,"E50");var subQ1=sQuery(id+"F2.wireOp",EDGE,"E36.right");var subQ2=sQuery(id+"F2.wireOp",EDGE,"E36.top");var subQ4=sQuery(id+"F0.wireOp",EDGE,"E0.top");var subQ5=sQuery(id+"F2.wireOp",EDGE,"E54");var subQ6=sQuery(id+"F2.wireOp",EDGE,"E48");var subQ7=sQuery(id+"F2.wireOp",EDGE,"E36.left");var subQ9=sQuery(id+"F2.wireOp",EDGE,"E47");var subQ10=sQuery(id+"F2.wireOp",EDGE,"E36.bottom");var subQ12=sQuery(id+"F2.wireOp",EDGE,"E46");var subQ13=sQuery(id+"F2.wireOp",EDGE,"E45");var subQ14=sQuery(id+"F2.wireOp",EDGE,"E44");var subQ15=sQuery(id+"F2.wireOp",EDGE,"E43");var subQ16=sQuery(id+"F2.wireOp",EDGE,"E42");var subQ17=sQuery(id+"F2.wireOp",EDGE,"E41");var subQ18=sQuery(id+"F2.wireOp",EDGE,"E40");var subQ19=sQuery(id+"F2.wireOp",EDGE,"E39");var subQ20=sQuery(id+"F2.wireOp",EDGE,"E51");var subQ21=sQuery(id+"F2.wireOp",EDGE,"E37");var subQ22=sQuery(id+"F2.wireOp",EDGE,"E38");var subQ23=sQuery(id+"F2.wireOp",EDGE,"E52");var subQ24=sQuery(id+"F2.wireOp",EDGE,"E53");Q0=makeQuery(id+"F16.boolean.opBoolean","SPLIT",FACE,{"disambiguationData":[TD([makeQuery(id+"F1.opExtrude","SWEPT_FACE",FACE,{"disambiguationData":[OSD([subQ4])]})])],"derivedFrom":makeQuery(id+"F3.opExtrude","CAP_FACE",FACE,{"disambiguationData":[OSD([subQ10,subQ2,subQ7,subQ1,subQ21,subQ22,subQ19,subQ18,subQ17,subQ16,subQ15,subQ14,subQ13,subQ12,subQ9,subQ6,subQ0,subQ20,subQ23,subQ24,subQ5])],"isStart":false})});}
            var sketch = newSketch(context, id + "F19", { "sketchPlane" : qUnion([Q0])});
            skLineSegment(sketch, "E72.bottom", {"start": v(-2, 48) * mm, "end": v(0, 48) * mm});
            skLineSegment(sketch, "E72.top", {"start": v(-2, 68.5) * mm, "end": v(0, 68.5) * mm});
            skLineSegment(sketch, "E72.left", {"start": v(-2, 48) * mm, "end": v(-2, 68.5) * mm});
            skLineSegment(sketch, "E72.right", {"start": v(0, 48) * mm, "end": v(0, 68.5) * mm});
            skSolve(sketch);
        }
        {
            var Q0;
            Q0=qSketchRegion(id+"F19",true);
            extrude(context, id + "F20", {"entities" : qUnion([Q0]), "operationType" : NewBodyOperationType.REMOVE, "oppositeDirection" : true, "depth" : 13 * mm, "offsetDistance" : 25 * mm});
        }
        {
            var Q0;
            {var subQ0=sQuery(id+"F2.wireOp",EDGE,"E36.left");var subQ1=sQuery(id+"F2.wireOp",EDGE,"E36.bottom");var subQ5=sQuery(id+"F2.wireOp",EDGE,"E46");var subQ7=sQuery(id+"F2.wireOp",EDGE,"E54");var subQ8=sQuery(id+"F2.wireOp",EDGE,"E48");var subQ10=sQuery(id+"F2.wireOp",EDGE,"E36.top");var subQ11=sQuery(id+"F0.wireOp",EDGE,"E0.top");var subQ13=sQuery(id+"F2.wireOp",EDGE,"E47");var subQ15=sQuery(id+"F2.wireOp",EDGE,"E45");var subQ17=sQuery(id+"F2.wireOp",EDGE,"E44");var subQ19=sQuery(id+"F2.wireOp",EDGE,"E43");var subQ21=sQuery(id+"F2.wireOp",EDGE,"E42");var subQ23=sQuery(id+"F2.wireOp",EDGE,"E41");var subQ25=sQuery(id+"F2.wireOp",EDGE,"E40");var subQ27=sQuery(id+"F2.wireOp",EDGE,"E39");var subQ30=makeQuery(id+"F1.opExtrude","SWEPT_FACE",FACE,{"disambiguationData":[OSD([subQ11])]});var subQ38=sQuery(id+"F2.wireOp",EDGE,"E36.right");var subQ40=sQuery(id+"F2.wireOp",EDGE,"E37");var subQ42=sQuery(id+"F2.wireOp",EDGE,"E38");var subQ45=sQuery(id+"F2.wireOp",EDGE,"E50");var subQ46=sQuery(id+"F2.wireOp",EDGE,"E51");var subQ47=sQuery(id+"F2.wireOp",EDGE,"E52");var subQ48=sQuery(id+"F2.wireOp",EDGE,"E53");Q0=makeQuery(id+"F20.boolean.opBoolean","SPLIT",FACE,{"disambiguationData":[TD([subQ30])],"derivedFrom":makeQuery(id+"F16.boolean.opBoolean","SPLIT",FACE,{"disambiguationData":[TD([subQ30])],"derivedFrom":makeQuery(id+"F3.opExtrude","CAP_FACE",FACE,{"disambiguationData":[OSD([subQ1,subQ10,subQ0,subQ38,subQ40,subQ42,subQ27,subQ25,subQ23,subQ21,subQ19,subQ17,subQ15,subQ5,subQ13,subQ8,subQ45,subQ46,subQ47,subQ48,subQ7])],"isStart":false})})});}
            var sketch = newSketch(context, id + "F21", { "sketchPlane" : qUnion([Q0])});
            skLineSegment(sketch, "E73.bottom", {"start": v(-2, 68.5) * mm, "end": v(0, 68.5) * mm});
            skLineSegment(sketch, "E73.top", {"start": v(-2, 87) * mm, "end": v(0, 87) * mm});
            skLineSegment(sketch, "E73.left", {"start": v(-2, 68.5) * mm, "end": v(-2, 87) * mm});
            skLineSegment(sketch, "E73.right", {"start": v(0, 68.5) * mm, "end": v(0, 87) * mm});
            skSolve(sketch);
        }
        {
            var Q0;
            Q0=qSketchRegion(id+"F21",true);
            extrude(context, id + "F22", {"entities" : qUnion([Q0]), "operationType" : NewBodyOperationType.REMOVE, "oppositeDirection" : true, "depth" : 22 * mm, "offsetDistance" : 25 * mm});
        }
        {
            var Q0;
            Q0=qCreatedBy(makeId("Top.planeOp"),FACE);
            var sketch = newSketch(context, id + "F23", { "sketchPlane" : qUnion([Q0])});
            skLineSegment(sketch, "E74.bottom", {"start": v(-231.5, -7.5) * mm, "end": v(7.5, -7.5) * mm});
            skLineSegment(sketch, "E74.top", {"start": v(-231.5, 151.5) * mm, "end": v(7.5, 151.5) * mm});
            skLineSegment(sketch, "E74.left", {"start": v(-231.5, -7.5) * mm, "end": v(-231.5, 151.5) * mm});
            skLineSegment(sketch, "E74.right", {"start": v(7.5, -7.5) * mm, "end": v(7.5, 151.5) * mm});
            skLineSegment(sketch, "E75.bottom", {"start": v(-232, -8) * mm, "end": v(8, -8) * mm});
            skLineSegment(sketch, "E75.top", {"start": v(-232, 152) * mm, "end": v(8, 152) * mm});
            skLineSegment(sketch, "E75.left", {"start": v(-232, -8) * mm, "end": v(-232, 152) * mm});
            skLineSegment(sketch, "E75.right", {"start": v(8, -8) * mm, "end": v(8, 152) * mm});
            skSolve(sketch);
        }
        {
            var Q0;
            Q0=qCreatedBy(makeId("Top.planeOp"),FACE);
            var sketch = newSketch(context, id + "F24", { "sketchPlane" : qUnion([Q0])});
            skLineSegment(sketch, "E76.bottom", {"start": v(-224, 0) * mm, "end": v(0, 0) * mm});
            skLineSegment(sketch, "E76.top", {"start": v(-224, 144) * mm, "end": v(0, 144) * mm});
            skLineSegment(sketch, "E76.left", {"start": v(-224, 0) * mm, "end": v(-224, 144) * mm});
            skLineSegment(sketch, "E76.right", {"start": v(0, 0) * mm, "end": v(0, 144) * mm});
            skSolve(sketch);
        }
        {
            var Q0;
            {var subQ0=sQuery(id+"F2.wireOp",EDGE,"E52");var subQ2=sQuery(id+"F2.wireOp",EDGE,"E36.right");var subQ3=sQuery(id+"F2.wireOp",EDGE,"E36.bottom");var subQ7=sQuery(id+"F2.wireOp",EDGE,"E51");var subQ10=sQuery(id+"F2.wireOp",EDGE,"E50");var subQ11=makeQuery(id+"F3.opExtrude","SWEPT_FACE",FACE,{"disambiguationData":[OSD([subQ10])]});var subQ12=sQuery(id+"F2.wireOp",EDGE,"E38");var subQ14=sQuery(id+"F2.wireOp",EDGE,"E53");var subQ20=sQuery(id+"F2.wireOp",EDGE,"E36.top");var subQ21=sQuery(id+"F0.wireOp",EDGE,"E0.top");var subQ22=sQuery(id+"F2.wireOp",EDGE,"E54");var subQ23=sQuery(id+"F2.wireOp",EDGE,"E48");var subQ24=sQuery(id+"F2.wireOp",EDGE,"E36.left");var subQ26=sQuery(id+"F2.wireOp",EDGE,"E47");var subQ27=sQuery(id+"F2.wireOp",EDGE,"E46");var subQ28=sQuery(id+"F2.wireOp",EDGE,"E45");var subQ29=sQuery(id+"F2.wireOp",EDGE,"E44");var subQ30=sQuery(id+"F2.wireOp",EDGE,"E43");var subQ31=sQuery(id+"F2.wireOp",EDGE,"E42");var subQ32=sQuery(id+"F2.wireOp",EDGE,"E41");var subQ33=sQuery(id+"F2.wireOp",EDGE,"E40");var subQ34=sQuery(id+"F2.wireOp",EDGE,"E39");var subQ35=sQuery(id+"F2.wireOp",EDGE,"E37");Q0=makeQuery(id+"F20.boolean.opBoolean","SPLIT",FACE,{"disambiguationData":[TD([subQ11])],"derivedFrom":makeQuery(id+"F16.boolean.opBoolean","SPLIT",FACE,{"disambiguationData":[TD([makeQuery(id+"F1.opExtrude","SWEPT_FACE",FACE,{"disambiguationData":[OSD([subQ21])]})])],"derivedFrom":makeQuery(id+"F3.opExtrude","CAP_FACE",FACE,{"disambiguationData":[OSD([subQ3,subQ20,subQ24,subQ2,subQ35,subQ12,subQ34,subQ33,subQ32,subQ31,subQ30,subQ29,subQ28,subQ27,subQ26,subQ23,subQ10,subQ7,subQ0,subQ14,subQ22])],"isStart":false})})});}
            var sketch = newSketch(context, id + "F25", { "sketchPlane" : qUnion([Q0])});
            skLineSegment(sketch, "E77.bottom", {"start": v(-96.4, 0) * mm, "end": v(-73.4, 0) * mm});
            skLineSegment(sketch, "E77.top", {"start": v(-96.4, 4) * mm, "end": v(-73.4, 4) * mm});
            skLineSegment(sketch, "E77.left", {"start": v(-96.4, 0) * mm, "end": v(-96.4, 4) * mm});
            skLineSegment(sketch, "E77.right", {"start": v(-73.4, 0) * mm, "end": v(-73.4, 4) * mm});
            skSolve(sketch);
        }
        {
            var Q0;
            Q0=qSketchRegion(id+"F25",true);
            extrude(context, id + "F26", {"entities" : qUnion([Q0]), "operationType" : NewBodyOperationType.REMOVE, "oppositeDirection" : true, "depth" : 22 * mm, "offsetDistance" : 25 * mm});
        }
        {
            var Q0;
            Q0=makeQuery(id+"F1.opExtrude","CAP_FACE",FACE,{"disambiguationData":[OSD([sQuery(id+"F0.wireOp",EDGE,"E0.bottom"),sQuery(id+"F0.wireOp",EDGE,"E0.top"),sQuery(id+"F0.wireOp",EDGE,"E0.left"),sQuery(id+"F0.wireOp",EDGE,"E0.right")])],"isStart":false});
            var sketch = newSketch(context, id + "F27", { "sketchPlane" : qUnion([Q0])});
            skLineSegment(sketch, "E78.bottom", {"start": v(-125.5, 4) * mm, "end": v(-12, 4) * mm});
            skLineSegment(sketch, "E78.top", {"start": v(-125.5, 132) * mm, "end": v(-12, 132) * mm});
            skLineSegment(sketch, "E78.left", {"start": v(-125.5, 4) * mm, "end": v(-125.5, 132) * mm});
            skLineSegment(sketch, "E78.right", {"start": v(-12, 4) * mm, "end": v(-12, 48) * mm});
            skLineSegment(sketch, "E79", {"start": v(-12, 87) * mm, "end": v(-2, 87) * mm});
            skLineSegment(sketch, "E80", {"start": v(-2, 87) * mm, "end": v(-2, 48) * mm});
            skLineSegment(sketch, "E81", {"start": v(-2, 48) * mm, "end": v(-12, 48) * mm});
            skLineSegment(sketch, "E82.trimOffspring", {"start": v(-12, 87) * mm, "end": v(-12, 132) * mm});
            skSolve(sketch);
        }
        {
            var Q0;
            Q0=qSketchRegion(id+"F27",true);
            extrude(context, id + "F28", {"entities" : qUnion([Q0]), "operationType" : NewBodyOperationType.ADD, "depth" : 2 * mm, "offsetDistance" : 25 * mm});
        }
    });
